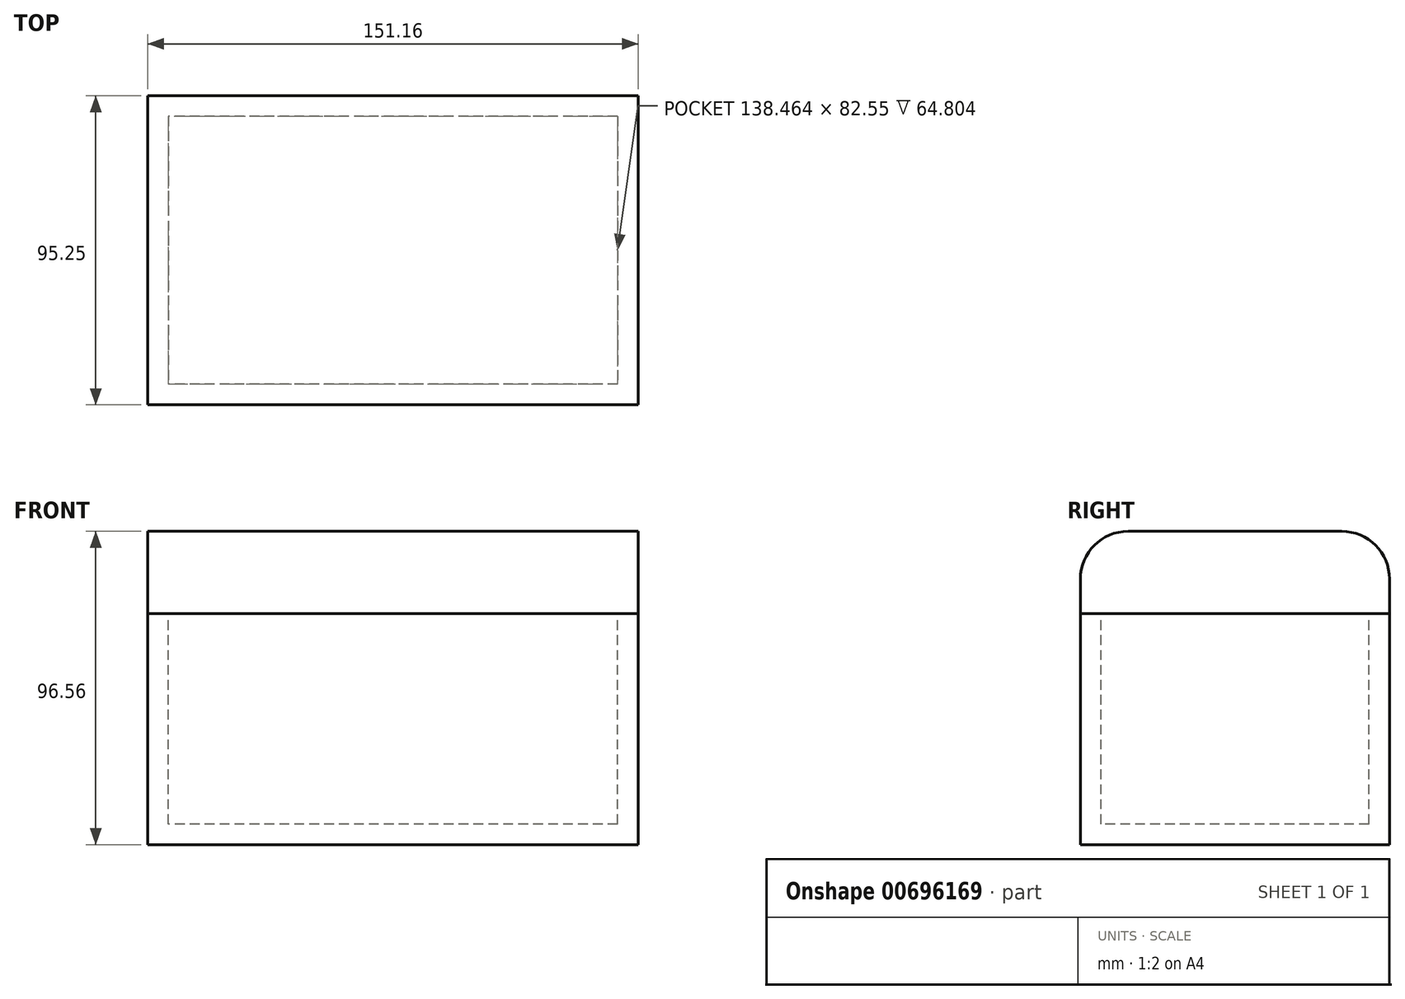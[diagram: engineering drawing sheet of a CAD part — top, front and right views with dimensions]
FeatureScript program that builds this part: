
annotation { "Feature Type Name" : "Feature", "Feature Type Description" : "" }
export const myFeature = defineFeature(function(context is Context, id is Id, definition is map)
    precondition{}
    {
        {
            var Q0;
            Q0=qCreatedBy(makeId("Front.planeOp"),FACE);
            var sketch = newSketch(context, id + "F0", { "sketchPlane" : qUnion([Q0])});
            skLineSegment(sketch, "E0.bottom", {"start": v(75.58, -35.58) * mm, "end": v(-75.58, -35.58) * mm});
            skLineSegment(sketch, "E0.top", {"start": v(75.58, 35.58) * mm, "end": v(-75.58, 35.58) * mm});
            skLineSegment(sketch, "E0.left", {"start": v(75.58, -35.58) * mm, "end": v(75.58, 35.58) * mm});
            skLineSegment(sketch, "E0.right", {"start": v(-75.58, -35.58) * mm, "end": v(-75.58, 35.58) * mm});
            skPoint(sketch, "E0.middle", {"position": v(0, 0) * mm});
            skSolve(sketch);
        }
        {
            var Q0;
            Q0=makeQuery(id+"F0.imprint","IMPRINT",FACE,{"disambiguationData":[TD([[makeQuery(id+"F0.imprint","IMPRINT",EDGE,{"derivedFrom":sQuery(id+"F0.wireOp",EDGE,"E0.bottom")}),-1.0]])]});
            extrude(context, id + "F1", {"entities" : qUnion([Q0]), "oppositeDirection" : true, "depth" : 95.25 * mm, "offsetDistance" : 25.4 * mm});
        }
        {
            var Q0;
            Q0=makeQuery(id+"F1.opExtrude","SWEPT_FACE",FACE,{"disambiguationData":[OSD([sQuery(id+"F0.wireOp",EDGE,"E0.top")])]});
            var sketch = newSketch(context, id + "F2", { "sketchPlane" : qUnion([Q0])});
            skSolve(sketch);
        }
        {
            var Q0;
            {var subQ0=sQuery(id+"F0.wireOp",EDGE,"E0.top");Q0=makeQuery(id+"F2.imprint","IMPRINT",FACE,{"disambiguationData":[TD([[makeQuery(id+"F2.imprint","IMPRINT",EDGE,{"derivedFrom":makeQuery(id+"F1.opExtrude","CAP_EDGE",EDGE,{"disambiguationData":[OSD([subQ0])],"isStart":true})}),-1.0]])]});}
            extrude(context, id + "F3", {"entities" : qUnion([Q0]), "depth" : 25.4 * mm, "offsetDistance" : 25.4 * mm});
        }
        {
            var Q0;
            {var subQ0=sQuery(id+"F0.wireOp",EDGE,"E0.top");Q0=makeQuery(id+"F3.opExtrude","CAP_EDGE",EDGE,{"disambiguationData":[OSD([subQ0]),TDD([makeQuery(id+"F2.imprint","IMPRINT",EDGE,{"derivedFrom":makeQuery(id+"F1.opExtrude","CAP_EDGE",EDGE,{"disambiguationData":[OSD([subQ0])],"isStart":true})})])],"isStart":false});}
            var Q1;
            {var subQ0=sQuery(id+"F0.wireOp",EDGE,"E0.top");Q1=makeQuery(id+"F3.opExtrude","CAP_EDGE",EDGE,{"disambiguationData":[OSD([subQ0]),TDD([makeQuery(id+"F2.imprint","IMPRINT",EDGE,{"derivedFrom":makeQuery(id+"F1.opExtrude","CAP_EDGE",EDGE,{"disambiguationData":[OSD([subQ0])],"isStart":false})})])],"isStart":false});}
            fillet(context, id + "F4", {"entities" : qUnion([Q0, Q1]), "radius" : 14.72 * mm, "tangentPropagation" : true, "allowEdgeOverflow" : false});
        }
        {
            var Q0;
            Q0=makeQuery(id+"F1.opExtrude","SWEPT_FACE",FACE,{"disambiguationData":[OSD([sQuery(id+"F0.wireOp",EDGE,"E0.top")])]});
            shell(context, id + "F5", {"entities" : qUnion([Q0]), "thickness" : 6.35 * mm});
        }
    });
